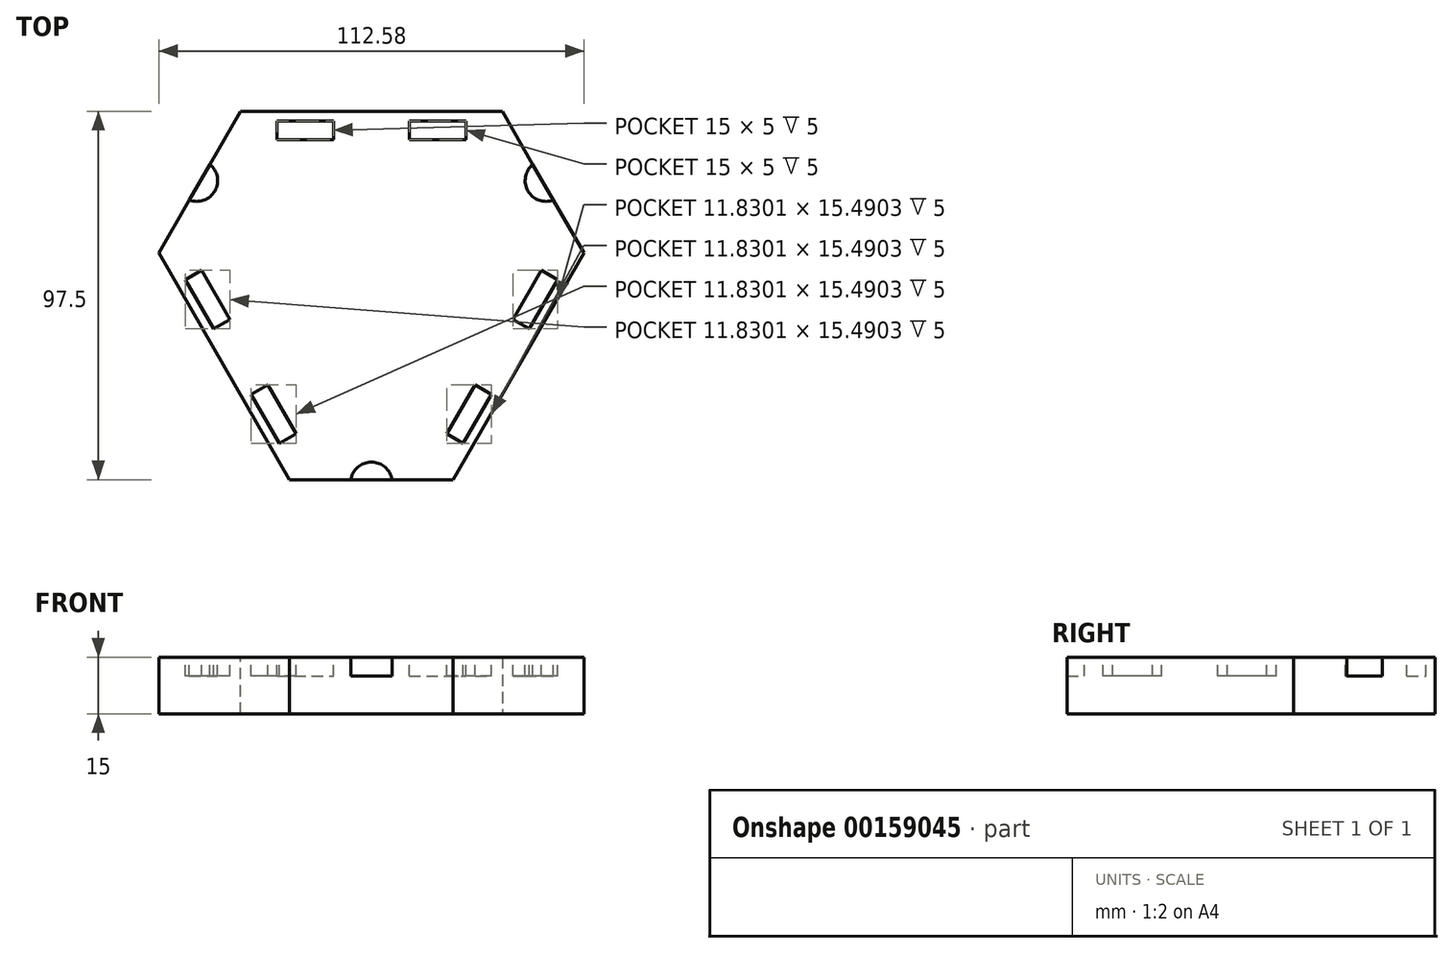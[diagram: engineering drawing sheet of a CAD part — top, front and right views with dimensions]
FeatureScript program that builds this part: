
annotation { "Feature Type Name" : "Feature", "Feature Type Description" : "" }
export const myFeature = defineFeature(function(context is Context, id is Id, definition is map)
    precondition{}
    {
        {
            var Q0;
            Q0=qCreatedBy(makeId("Top.planeOp"),FACE);
            var sketch = newSketch(context, id + "F0", { "sketchPlane" : qUnion([Q0])});
            skCircle(sketch, "E0.cCircle", {"center": v(0, 0) * mm, "radius": 90 * mm, "construction": true});
            skLineSegment(sketch, "E0.0", {"start": v(0, -90) * mm, "end": v(-77.94, 45) * mm});
            skLineSegment(sketch, "E0.1", {"start": v(-77.94, 45) * mm, "end": v(77.94, 45) * mm});
            skLineSegment(sketch, "E0.2", {"start": v(77.94, 45) * mm, "end": v(0, -90) * mm});
            skSolve(sketch);
        }
        {
            var Q0;
            Q0=qSketchRegion(id+"F0",true);
            extrude(context, id + "F1", {"entities" : qUnion([Q0]), "depth" : 15 * mm});
        }
        {
            var Q0;
            Q0=makeQuery(id+"F1.opExtrude","SWEPT_EDGE",EDGE,{"disambiguationData":[OSD([sQuery(id+"F0.wireOp",EDGE,"E0.0"),sQuery(id+"F0.wireOp",EDGE,"E0.2")])]});
            var Q1;
            Q1=makeQuery(id+"F1.opExtrude","SWEPT_EDGE",EDGE,{"disambiguationData":[OSD([sQuery(id+"F0.wireOp",EDGE,"E0.1"),sQuery(id+"F0.wireOp",EDGE,"E0.2")])]});
            var Q2;
            Q2=makeQuery(id+"F1.opExtrude","SWEPT_EDGE",EDGE,{"disambiguationData":[OSD([sQuery(id+"F0.wireOp",EDGE,"E0.0"),sQuery(id+"F0.wireOp",EDGE,"E0.1")])]});
            chamfer(context, id + "F2", {"entities" : qUnion([Q0, Q1, Q2]), "width" : 25 * mm, "tangentPropagation" : true});
        }
        {
            var Q0;
            Q0=makeQuery(id+"F1.opExtrude","CAP_FACE",FACE,{"disambiguationData":[OSD([sQuery(id+"F0.wireOp",EDGE,"E0.0"),sQuery(id+"F0.wireOp",EDGE,"E0.1"),sQuery(id+"F0.wireOp",EDGE,"E0.2")])],"isStart":false});
            var sketch = newSketch(context, id + "F3", { "sketchPlane" : qUnion([Q0])});
            skLineSegment(sketch, "E1.bottom", {"start": v(-25, 37.5) * mm, "end": v(-10, 37.5) * mm});
            skLineSegment(sketch, "E1.top", {"start": v(-25, 42.5) * mm, "end": v(-10, 42.5) * mm});
            skLineSegment(sketch, "E1.left", {"start": v(-25, 37.5) * mm, "end": v(-25, 42.5) * mm});
            skLineSegment(sketch, "E1.right", {"start": v(25, 37.5) * mm, "end": v(25, 42.5) * mm});
            skPoint(sketch, "E1.middle", {"position": v(0, 40) * mm});
            skLineSegment(sketch, "E2.left", {"start": v(-10, 37.5) * mm, "end": v(-10, 42.5) * mm});
            skLineSegment(sketch, "E2.right", {"start": v(10, 37.5) * mm, "end": v(10, 42.5) * mm});
            skLineSegment(sketch, "E3.trimOffspring", {"start": v(10, 42.5) * mm, "end": v(25, 42.5) * mm});
            skLineSegment(sketch, "E4.trimOffspring", {"start": v(10, 37.5) * mm, "end": v(25, 37.5) * mm});
            skLineSegment(sketch, "E5.1.0", {"start": v(49.3, 0.4) * mm, "end": v(41.8, -12.59) * mm});
            skPoint(sketch, "E5.1.1", {"position": v(34.64, -20) * mm});
            skLineSegment(sketch, "E5.1.2", {"start": v(27.48, -27.41) * mm, "end": v(19.98, -40.4) * mm});
            skLineSegment(sketch, "E5.1.3", {"start": v(31.8, -29.91) * mm, "end": v(24.3, -42.9) * mm});
            skLineSegment(sketch, "E5.1.4", {"start": v(44.98, 2.9) * mm, "end": v(37.48, -10.09) * mm});
            skPoint(sketch, "E5.1.5", {"position": v(34.64, -20) * mm});
            skLineSegment(sketch, "E5.1.6", {"start": v(44.98, 2.9) * mm, "end": v(49.3, 0.4) * mm});
            skLineSegment(sketch, "E5.1.7", {"start": v(19.98, -40.4) * mm, "end": v(24.3, -42.9) * mm});
            skLineSegment(sketch, "E5.1.8", {"start": v(27.48, -27.41) * mm, "end": v(31.8, -29.91) * mm});
            skLineSegment(sketch, "E5.1.9", {"start": v(37.48, -10.09) * mm, "end": v(41.8, -12.59) * mm});
            skLineSegment(sketch, "E5.2.0", {"start": v(-24.3, -42.9) * mm, "end": v(-31.8, -29.91) * mm});
            skPoint(sketch, "E5.2.1", {"position": v(-34.64, -20) * mm});
            skLineSegment(sketch, "E5.2.2", {"start": v(-37.48, -10.09) * mm, "end": v(-44.98, 2.9) * mm});
            skLineSegment(sketch, "E5.2.3", {"start": v(-41.8, -12.59) * mm, "end": v(-49.3, 0.4) * mm});
            skLineSegment(sketch, "E5.2.4", {"start": v(-19.98, -40.4) * mm, "end": v(-27.48, -27.41) * mm});
            skPoint(sketch, "E5.2.5", {"position": v(-34.64, -20) * mm});
            skLineSegment(sketch, "E5.2.6", {"start": v(-19.98, -40.4) * mm, "end": v(-24.3, -42.9) * mm});
            skLineSegment(sketch, "E5.2.7", {"start": v(-44.98, 2.9) * mm, "end": v(-49.3, 0.4) * mm});
            skLineSegment(sketch, "E5.2.8", {"start": v(-37.48, -10.09) * mm, "end": v(-41.8, -12.59) * mm});
            skLineSegment(sketch, "E5.2.9", {"start": v(-27.48, -27.41) * mm, "end": v(-31.8, -29.91) * mm});
            skPoint(sketch, "E5.center", {"position": v(0, 0) * mm});
            skLineSegment(sketch, "E5.anchor1", {"start": v(0, 0) * mm, "end": v(-25, 37.5) * mm, "construction": true});
            skLineSegment(sketch, "E5.anchor2", {"start": v(0, 0) * mm, "end": v(-19.98, -40.4) * mm, "construction": true});
            skSolve(sketch);
        }
        {
            var Q0;
            Q0=qSketchRegion(id+"F3",true);
            extrude(context, id + "F4", {"entities" : qUnion([Q0]), "operationType" : NewBodyOperationType.REMOVE, "oppositeDirection" : true, "depth" : 5 * mm});
        }
        {
            var Q0;
            Q0=makeQuery(id+"F1.opExtrude","CAP_FACE",FACE,{"disambiguationData":[OSD([sQuery(id+"F0.wireOp",EDGE,"E0.0"),sQuery(id+"F0.wireOp",EDGE,"E0.1"),sQuery(id+"F0.wireOp",EDGE,"E0.2")])],"isStart":false});
            var sketch = newSketch(context, id + "F5", { "sketchPlane" : qUnion([Q0])});
            skCircle(sketch, "E6", {"center": v(0, -53.35) * mm, "radius": 5.5 * mm});
            skCircle(sketch, "E7.1.0", {"center": v(-46.2, 26.67) * mm, "radius": 5.5 * mm});
            skCircle(sketch, "E7.2.0", {"center": v(46.2, 26.67) * mm, "radius": 5.5 * mm});
            skPoint(sketch, "E7.center", {"position": v(0, 0) * mm});
            skLineSegment(sketch, "E7.anchor1", {"start": v(0, 0) * mm, "end": v(0, -53.35) * mm, "construction": true});
            skLineSegment(sketch, "E7.anchor2", {"start": v(0, 0) * mm, "end": v(46.2, 26.67) * mm, "construction": true});
            skSolve(sketch);
        }
        {
            var Q0;
            Q0 = qSketchRegion(id + "F5", true);
            extrude(context, id + "F6", {"entities" : qUnion([Q0]), "operationType" : NewBodyOperationType.REMOVE, "oppositeDirection" : true, "depth" : 5 * mm});
        }
    });
